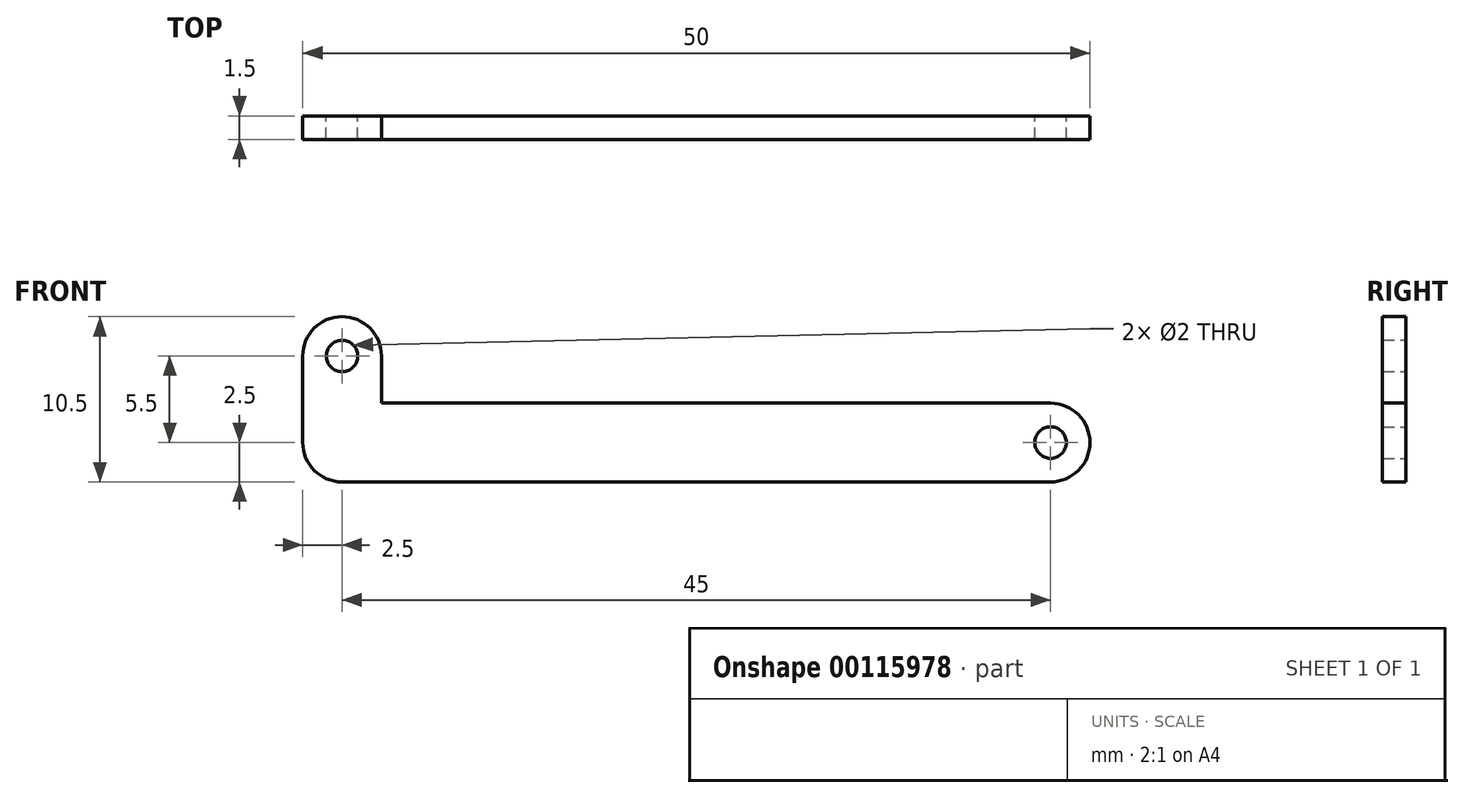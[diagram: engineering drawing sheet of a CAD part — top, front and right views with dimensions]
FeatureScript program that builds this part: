
annotation { "Feature Type Name" : "Feature", "Feature Type Description" : "" }
export const myFeature = defineFeature(function(context is Context, id is Id, definition is map)
    precondition{}
    {
        {
            var Q0;
            Q0=qCreatedBy(makeId("Front.planeOp"),FACE);
            var sketch = newSketch(context, id + "F0", { "sketchPlane" : qUnion([Q0])});
            skLineSegment(sketch, "E0.bottom", {"start": v(0, 0) * mm, "end": v(22.5, 0) * mm});
            skLineSegment(sketch, "E0.top", {"start": v(0, 5) * mm, "end": v(22.5, 5) * mm});
            skLineSegment(sketch, "E0.left", {"start": v(0, 0) * mm, "end": v(0, 5) * mm, "construction": true});
            skLineSegment(sketch, "E0.right", {"start": v(25, 2.5) * mm, "end": v(25, 2.5) * mm});
            skPoint(sketch, "E1.visualSharp", {"position": v(25, 5) * mm});
            skArc(sketch, "E1.filletArc", {"start": v(25, 2.5) * mm, "mid": v(24.27, 4.27) * mm, "end": v(22.5, 5) * mm});
            skPoint(sketch, "E2.visualSharp", {"position": v(25, 0) * mm});
            skArc(sketch, "E2.filletArc", {"start": v(22.5, 0) * mm, "mid": v(24.27, 0.73) * mm, "end": v(25, 2.5) * mm});
            skCircle(sketch, "E3", {"center": v(22.5, 2.5) * mm, "radius": 1 * mm});
            skPoint(sketch, "E4.MirrorP", {"position": v(-25, 0) * mm});
            skLineSegment(sketch, "E5.MirrorCS", {"start": v(0, 0) * mm, "end": v(-22.5, 0) * mm});
            skLineSegment(sketch, "E6.MirrorCS", {"start": v(0, 5) * mm, "end": v(-20, 5) * mm});
            skArc(sketch, "E7.MirrorCS", {"start": v(-22.5, 0) * mm, "mid": v(-24.27, 0.73) * mm, "end": v(-25, 2.5) * mm});
            skLineSegment(sketch, "E8", {"start": v(-25, 2.5) * mm, "end": v(-25, 8) * mm});
            skLineSegment(sketch, "E9", {"start": v(-22.5, 10.5) * mm, "end": v(-22.5, 10.5) * mm});
            skLineSegment(sketch, "E10", {"start": v(-20, 8) * mm, "end": v(-20, 5) * mm});
            skLineSegment(sketch, "E11", {"start": v(-20, 5) * mm, "end": v(-25, 5) * mm, "construction": true});
            skPoint(sketch, "E12.visualSharp", {"position": v(-25, 10.5) * mm});
            skArc(sketch, "E12.filletArc", {"start": v(-22.5, 10.5) * mm, "mid": v(-24.27, 9.77) * mm, "end": v(-25, 8) * mm});
            skPoint(sketch, "E13.visualSharp", {"position": v(-20, 10.5) * mm});
            skArc(sketch, "E13.filletArc", {"start": v(-20, 8) * mm, "mid": v(-20.73, 9.77) * mm, "end": v(-22.5, 10.5) * mm});
            skCircle(sketch, "E14", {"center": v(-22.5, 8) * mm, "radius": 1 * mm});
            skSolve(sketch);
        }
        {
            var Q0;
            Q0 = qSketchRegion(id + "F0", true);
            extrude(context, id + "F1", {"entities" : qUnion([Q0]), "endBound" : BoundingType.SYMMETRIC, "depth" : 1.5 * mm});
        }
    });
